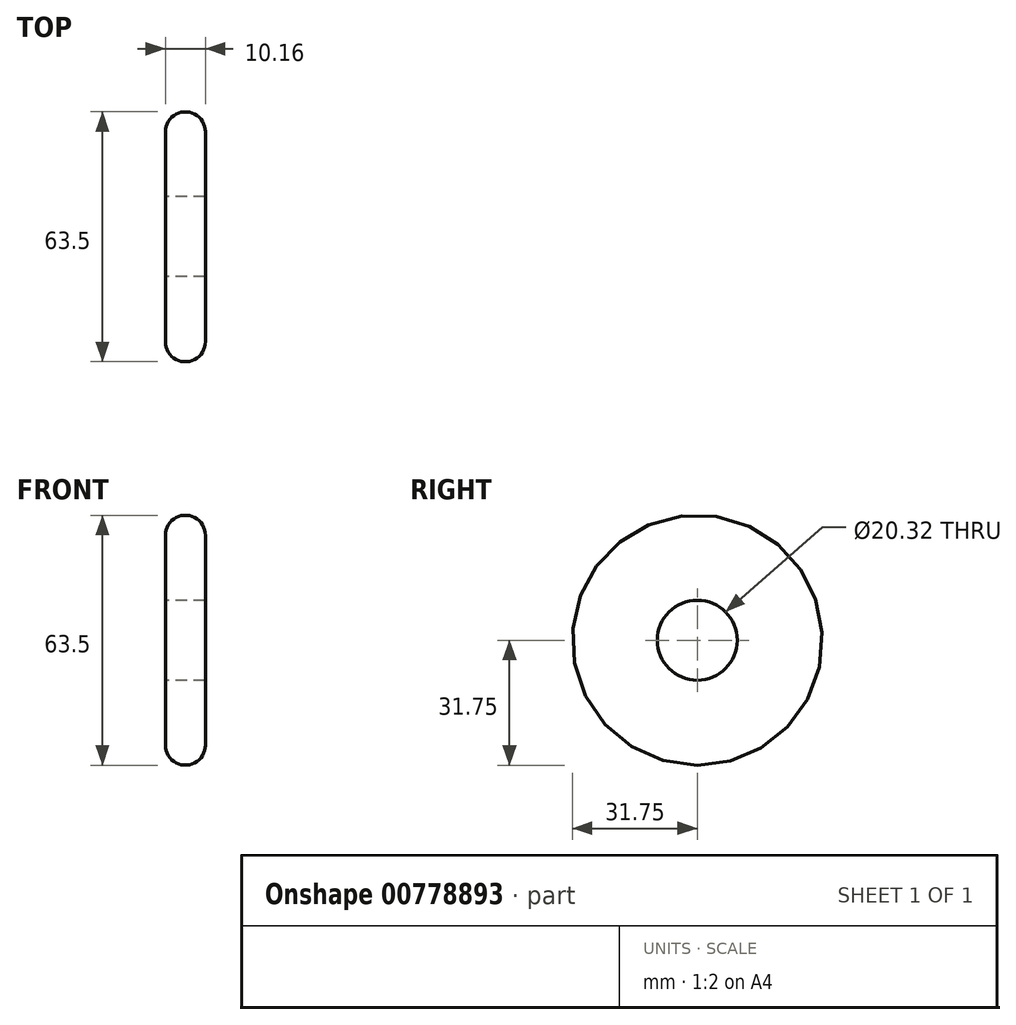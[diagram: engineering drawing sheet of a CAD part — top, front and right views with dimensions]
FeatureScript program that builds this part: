
annotation { "Feature Type Name" : "Feature", "Feature Type Description" : "" }
export const myFeature = defineFeature(function(context is Context, id is Id, definition is map)
    precondition{}
    {
        {
            var Q0;
            Q0=qCreatedBy(makeId("Right.planeOp"),FACE);
            var sketch = newSketch(context, id + "F0", { "sketchPlane" : qUnion([Q0])});
            skCircle(sketch, "E0", {"center": v(0, 0) * mm, "radius": 31.75 * mm});
            skSolve(sketch);
        }
        {
            var Q0;
            Q0=qCreatedBy(makeId("Right.planeOp"),FACE);
            var sketch = newSketch(context, id + "F1", { "sketchPlane" : qUnion([Q0])});
            skCircle(sketch, "E1", {"center": v(0, 0) * mm, "radius": 10.16 * mm});
            skSolve(sketch);
        }
        {
            var Q0;
            Q0=makeQuery(id+"F0.imprint","IMPRINT",FACE,{"disambiguationData":[TD([[makeQuery(id+"F0.imprint","IMPRINT",EDGE,{"derivedFrom":sQuery(id+"F0.wireOp",EDGE,"E0")}),1.0]])]});
            extrude(context, id + "F2", {"entities" : qUnion([Q0]), "depth" : 10.16 * mm, "offsetDistance" : 25.4 * mm});
        }
        {
            var Q0;
            Q0=sQuery(id+"F1.wireOp",VERTEX,"E1.center");
            var Q1;
            Q1=makeQuery(id+"F2.opExtrude","SWEPT_BODY",BODY,{"disambiguationData":[OSD([sQuery(id+"F0.wireOp",EDGE,"E0")])]});
            hole(context, id + "F3", {"style" : HoleStyle.SIMPLE, "endStyle" : HoleEndStyle.THROUGH, "oppositeDirection" : true, "holeDiameter" : 20.32 * mm, "majorDiameter" : 6.35 * mm, "isTappedThrough" : true, "tappedDepth" : 12.7 * mm, "tapClearance" : 3, "locations" : qUnion([Q0]), "scope" : qUnion([Q1])});
        }
        {
            var Q0;
            Q0=makeQuery(id+"F2.opExtrude","CAP_EDGE",EDGE,{"disambiguationData":[OSD([sQuery(id+"F0.wireOp",EDGE,"E0")])],"isStart":true});
            fillet(context, id + "F4", {"entities" : qUnion([Q0]), "radius" : 5.08 * mm, "tangentPropagation" : true, "allowEdgeOverflow" : false});
        }
        {
            var Q0;
            Q0=makeQuery(id+"F2.opExtrude","CAP_EDGE",EDGE,{"disambiguationData":[OSD([sQuery(id+"F0.wireOp",EDGE,"E0")])],"isStart":false});
            fillet(context, id + "F5", {"entities" : qUnion([Q0]), "radius" : 5.08 * mm, "tangentPropagation" : true, "allowEdgeOverflow" : false});
        }
    });
